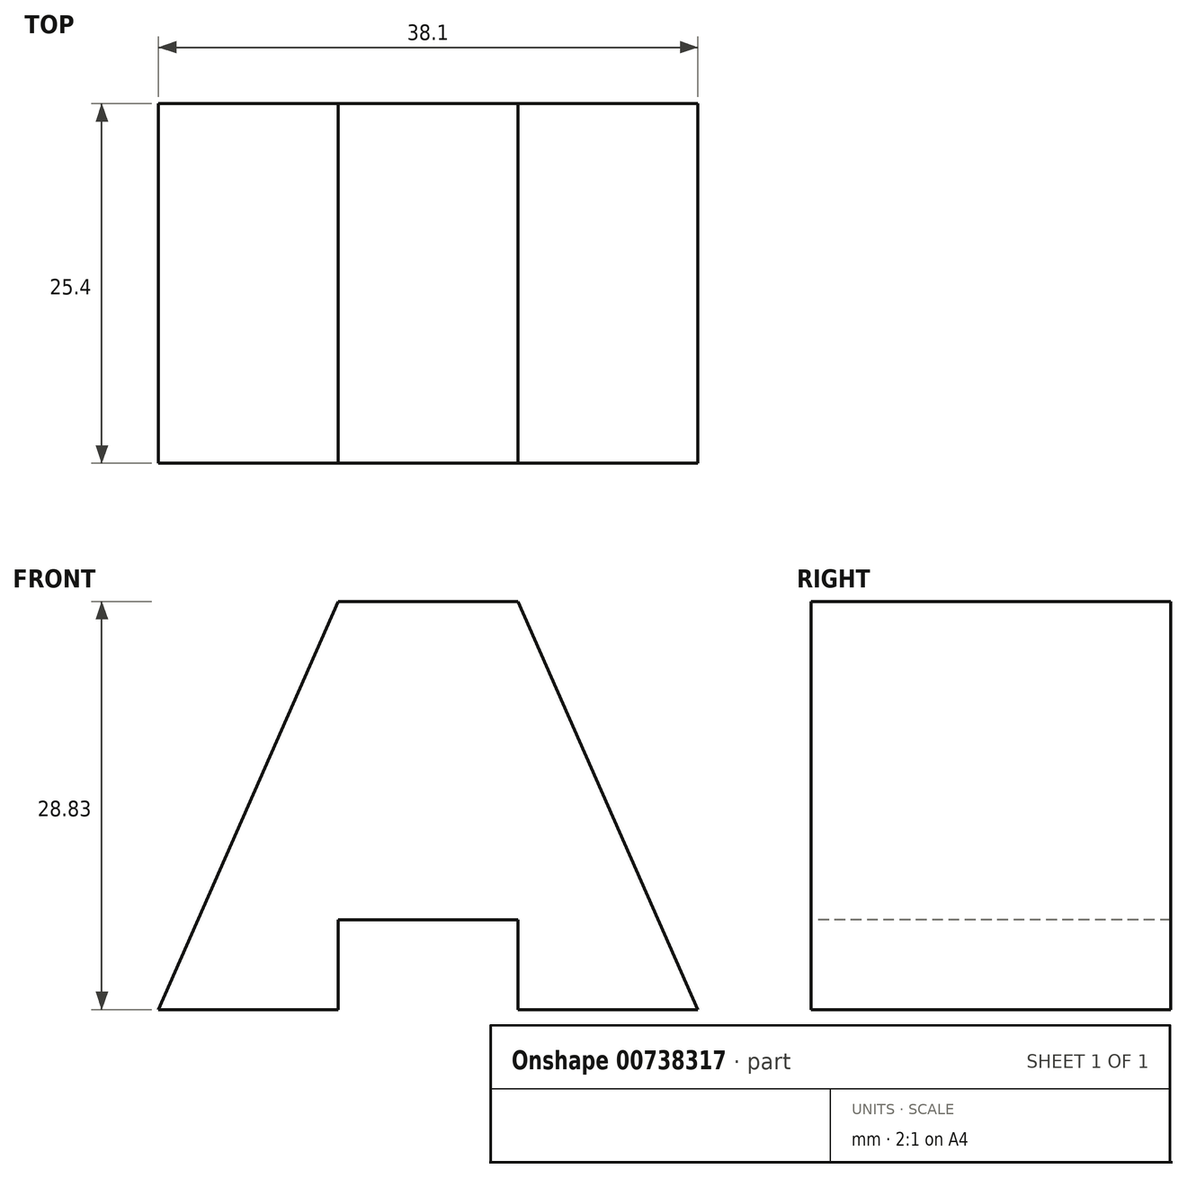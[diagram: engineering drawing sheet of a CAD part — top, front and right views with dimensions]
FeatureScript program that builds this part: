
annotation { "Feature Type Name" : "Feature", "Feature Type Description" : "" }
export const myFeature = defineFeature(function(context is Context, id is Id, definition is map)
    precondition{}
    {
        {
            var Q0;
            Q0=qCreatedBy(makeId("Front.planeOp"),FACE);
            var sketch = newSketch(context, id + "F0", { "sketchPlane" : qUnion([Q0])});
            skLineSegment(sketch, "E0", {"start": v(-25.4, 0) * mm, "end": v(-12.7, 28.83) * mm});
            skLineSegment(sketch, "E1", {"start": v(-12.7, 28.83) * mm, "end": v(0, 28.83) * mm});
            skLineSegment(sketch, "E2", {"start": v(0, 28.83) * mm, "end": v(12.7, 0) * mm});
            skLineSegment(sketch, "E3", {"start": v(12.7, 0) * mm, "end": v(-25.4, 0) * mm});
            skLineSegment(sketch, "E4", {"start": v(0, 0) * mm, "end": v(12.7, 0) * mm});
            skLineSegment(sketch, "E5", {"start": v(0, 0) * mm, "end": v(-25.4, 0) * mm});
            skSolve(sketch);
        }
        {
            var Q0;
            {var subQ1=sQuery(id+"F0.wireOp",EDGE,"E0");Q0=makeQuery(id+"F0.imprint","IMPRINT",FACE,{"disambiguationData":[TD([[makeQuery(id+"F0.imprint","IMPRINT",EDGE,{"derivedFrom":subQ1}),-1.0]])]});}
            extrude(context, id + "F1", {"entities" : qUnion([Q0]), "depth" : 25.4 * mm, "offsetDistance" : 25.4 * mm});
        }
        {
            var Q0;
            Q0=makeQuery(id+"F1.opExtrude","CAP_FACE",FACE,{"disambiguationData":[OSD([sQuery(id+"F0.wireOp",EDGE,"E0"),sQuery(id+"F0.wireOp",EDGE,"E1"),sQuery(id+"F0.wireOp",EDGE,"E2"),sQuery(id+"F0.wireOp",EDGE,"E3")])],"isStart":false});
            var sketch = newSketch(context, id + "F2", { "sketchPlane" : qUnion([Q0])});
            skLineSegment(sketch, "E6", {"start": v(-12.7, 0) * mm, "end": v(-12.7, 6.35) * mm});
            skLineSegment(sketch, "E7", {"start": v(-12.7, 6.35) * mm, "end": v(0, 6.35) * mm});
            skLineSegment(sketch, "E8", {"start": v(0, 6.35) * mm, "end": v(0, 0) * mm});
            skLineSegment(sketch, "E9", {"start": v(0, 0) * mm, "end": v(12.7, 0) * mm});
            skSolve(sketch);
        }
        {
            var Q0;
            {var subQ0=sQuery(id+"F2.wireOp",EDGE,"E6");Q0=makeQuery(id+"F2.imprint","IMPRINT",FACE,{"disambiguationData":[TD([[makeQuery(id+"F2.imprint","IMPRINT",EDGE,{"derivedFrom":subQ0}),-1.0]])]});}
            extrude(context, id + "F3", {"entities" : qUnion([Q0]), "operationType" : NewBodyOperationType.REMOVE, "endBound" : BoundingType.THROUGH_ALL, "oppositeDirection" : true, "depth" : 25.4 * mm, "offsetDistance" : 25.4 * mm});
        }
    });
